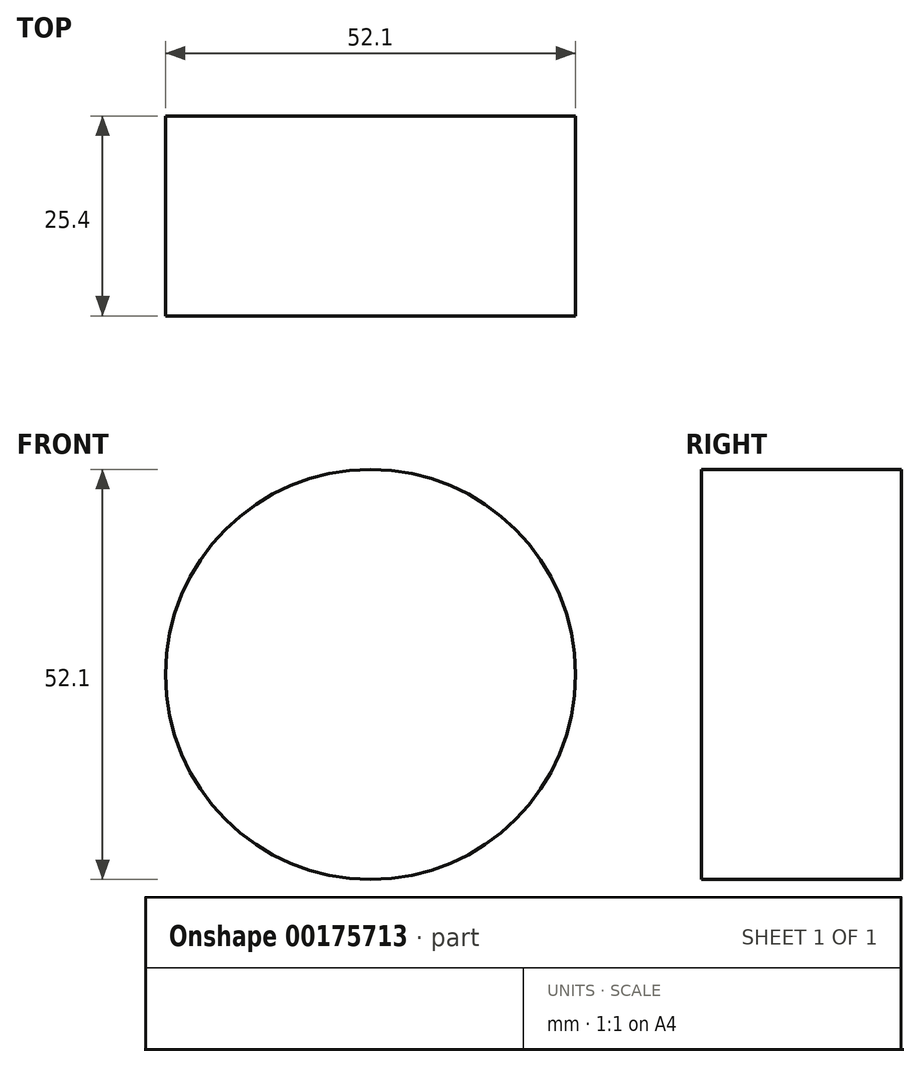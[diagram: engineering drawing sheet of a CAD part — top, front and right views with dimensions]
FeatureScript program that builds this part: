
annotation { "Feature Type Name" : "Feature", "Feature Type Description" : "" }
export const myFeature = defineFeature(function(context is Context, id is Id, definition is map)
    precondition{}
    {
        {
            var Q0;
            Q0=qCreatedBy(makeId("Front.planeOp"),FACE);
            var sketch = newSketch(context, id + "F0", { "sketchPlane" : qUnion([Q0])});
            skCircle(sketch, "E0", {"center": v(0, 0) * mm, "radius": 26.05 * mm});
            skSolve(sketch);
        }
        {
            var Q0;
            Q0=sQuery(id+"F0.wireOp",EDGE,"E0");
            extrude(context, id + "F1", {"bodyType" : ToolBodyType.SURFACE, "surfaceEntities" : qUnion([Q0]), "depth" : 25.4 * mm});
        }
    });
